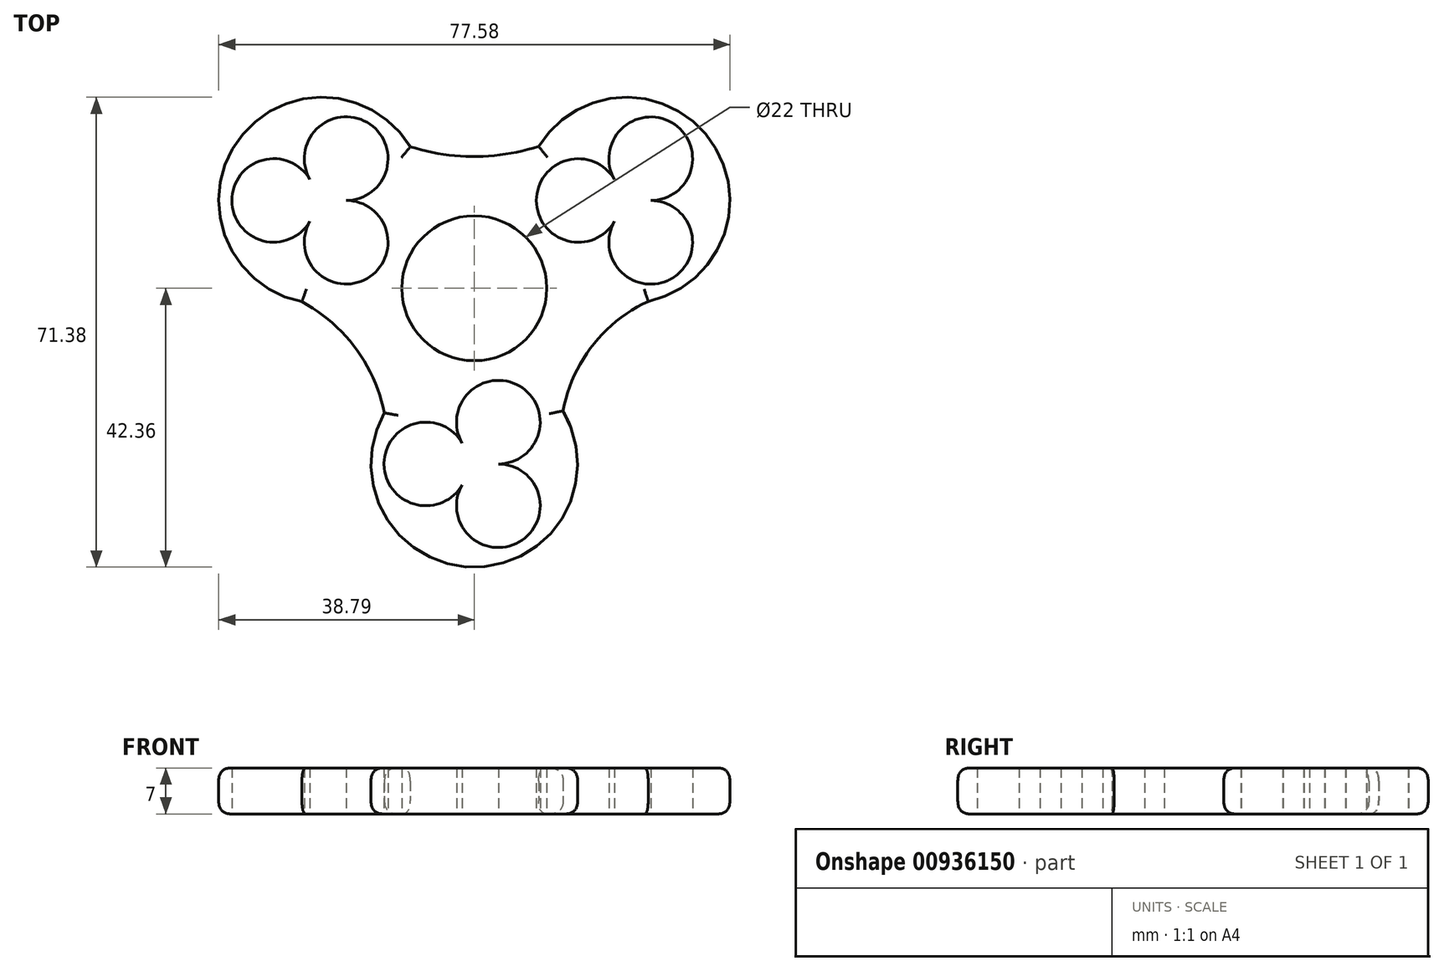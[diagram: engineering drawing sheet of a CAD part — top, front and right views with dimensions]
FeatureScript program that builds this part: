
annotation { "Feature Type Name" : "Feature", "Feature Type Description" : "" }
export const myFeature = defineFeature(function(context is Context, id is Id, definition is map)
    precondition{}
    {
        {
            var Q0;
            Q0=qCreatedBy(makeId("Top.planeOp"),FACE);
            var sketch = newSketch(context, id + "F0", { "sketchPlane" : qUnion([Q0])});
            skCircle(sketch, "E0", {"center": v(0, 0) * mm, "radius": 11 * mm});
            skPoint(sketch, "E1", {"position": v(0, -26.68) * mm});
            skCircle(sketch, "E2", {"center": v(0, -26.68) * mm, "radius": 13.68 * mm});
            skCircle(sketch, "E3.1.0", {"center": v(23.1, 13.34) * mm, "radius": 13.68 * mm});
            skCircle(sketch, "E3.2.0", {"center": v(-23.1, 13.34) * mm, "radius": 13.68 * mm});
            skCircle(sketch, "E4", {"center": v(0, -26.68) * mm, "radius": 15.68 * mm});
            skCircle(sketch, "E5.1.0", {"center": v(23.1, 13.34) * mm, "radius": 15.68 * mm});
            skCircle(sketch, "E5.2.0", {"center": v(-23.1, 13.34) * mm, "radius": 15.68 * mm});
            skPoint(sketch, "E6.endSnap0", {"position": v(0, 13.34) * mm});
            skArc(sketch, "E7", {"start": v(-9.72, 21.5) * mm, "mid": v(0.02, 20.01) * mm, "end": v(9.75, 21.56) * mm});
            skArc(sketch, "E8", {"start": v(26.39, -2) * mm, "mid": v(17.9, -8.75) * mm, "end": v(13.46, -18.64) * mm});
            skArc(sketch, "E9", {"start": v(-13.64, -18.94) * mm, "mid": v(-18.02, -9.1) * mm, "end": v(-26.15, -2.04) * mm});
            skPoint(sketch, "E10.end.orphan", {"position": v(30.3, 13.34) * mm});
            skPoint(sketch, "E6.end.orphan", {"position": v(7.43, 13.34) * mm});
            skPoint(sketch, "E11", {"position": v(6.84, -26.68) * mm});
            skPoint(sketch, "E12", {"position": v(-3.42, -32.6) * mm});
            skPoint(sketch, "E13", {"position": v(-2.54, -23.28) * mm});
            skPoint(sketch, "E14.center.orphan", {"position": v(-2.54, -26.17) * mm});
            skPoint(sketch, "E15.end.orphan", {"position": v(13.68, -26.68) * mm});
            skPoint(sketch, "E16.end.orphan", {"position": v(-6.84, -38.53) * mm});
            skLineSegment(sketch, "E17", {"start": v(-36.79, 13.34) * mm, "end": v(-23.1, 13.34) * mm});
            skPoint(sketch, "E18", {"position": v(-30.44, 13.34) * mm});
            skCircle(sketch, "E19", {"center": v(-30.44, 13.34) * mm, "radius": 6.35 * mm});
            skLineSegment(sketch, "E20", {"start": v(-23.1, 13.34) * mm, "end": v(-16.23, 25.25) * mm});
            skLineSegment(sketch, "E21", {"start": v(-23.1, 13.34) * mm, "end": v(-16.27, 1.5) * mm});
            skPoint(sketch, "E22", {"position": v(-19.44, 19.7) * mm});
            skPoint(sketch, "E23", {"position": v(-19.44, 7) * mm});
            skCircle(sketch, "E24", {"center": v(-19.44, 7) * mm, "radius": 6.35 * mm});
            skCircle(sketch, "E25", {"center": v(-19.44, 19.7) * mm, "radius": 6.35 * mm});
            skCircle(sketch, "E26.1.0", {"center": v(-7.35, -26.7) * mm, "radius": 6.35 * mm});
            skCircle(sketch, "E26.1.1", {"center": v(3.65, -33.04) * mm, "radius": 6.35 * mm});
            skCircle(sketch, "E26.1.2", {"center": v(3.65, -20.34) * mm, "radius": 6.35 * mm});
            skCircle(sketch, "E26.2.0", {"center": v(26.77, 6.97) * mm, "radius": 6.35 * mm});
            skCircle(sketch, "E26.2.1", {"center": v(26.77, 19.67) * mm, "radius": 6.35 * mm});
            skCircle(sketch, "E26.2.2", {"center": v(15.77, 13.32) * mm, "radius": 6.35 * mm});
            skSolve(sketch);
        }
        {
            var Q0;
            {var subQ4=sQuery(id+"F0.wireOp",EDGE,"E5.2.0");var subQ5=makeQuery(id+"F0.imprint","INTERSECT",VERTEX,{"derivedFrom":[subQ4,sQuery(id+"F0.wireOp",EDGE,"E9")]});Q0=makeQuery(id+"F0.imprint","IMPRINT",FACE,{"disambiguationData":[TD([[makeQuery(id+"F0.imprint","IMPRINT",EDGE,{"disambiguationData":[TD([[subQ5,-1.0]])],"derivedFrom":subQ4}),1.0]])]});}
            var Q1;
            {var subQ0=sQuery(id+"F0.wireOp",EDGE,"E19");var subQ1=sQuery(id+"F0.wireOp",EDGE,"E3.2.0");var subQ2=makeQuery(id+"F0.imprint","INTERSECT",VERTEX,{"disambiguationData":[OD(0.0)],"derivedFrom":[subQ1,subQ0]});Q1=makeQuery(id+"F0.imprint","IMPRINT",FACE,{"disambiguationData":[TD([[makeQuery(id+"F0.imprint","IMPRINT",EDGE,{"disambiguationData":[TD([[subQ2,1.0]])],"derivedFrom":subQ0}),-1.0]])]});}
            var Q2;
            {var subQ0=sQuery(id+"F0.wireOp",EDGE,"E24");var subQ3=sQuery(id+"F0.wireOp",EDGE,"E25");var subQ5=makeQuery(id+"F0.imprint","INTERSECT",VERTEX,{"derivedFrom":[subQ0,subQ3]});Q2=makeQuery(id+"F0.imprint","IMPRINT",FACE,{"disambiguationData":[TD([[makeQuery(id+"F0.imprint","IMPRINT",EDGE,{"disambiguationData":[TD([[subQ5,1.0]])],"derivedFrom":subQ0}),-1.0]])]});}
            var Q3;
            {var subQ1=sQuery(id+"F0.wireOp",EDGE,"E3.2.0");var subQ3=sQuery(id+"F0.wireOp",EDGE,"E19");var subQ4=makeQuery(id+"F0.imprint","INTERSECT",VERTEX,{"disambiguationData":[OD(1.0)],"derivedFrom":[subQ1,subQ3]});Q3=makeQuery(id+"F0.imprint","IMPRINT",FACE,{"disambiguationData":[TD([[makeQuery(id+"F0.imprint","IMPRINT",EDGE,{"disambiguationData":[TD([[subQ4,-1.0]])],"derivedFrom":subQ3}),-1.0]])]});}
            var Q4;
            {var subQ0=sQuery(id+"F0.wireOp",EDGE,"E7");Q4=makeQuery(id+"F0.imprint","IMPRINT",FACE,{"disambiguationData":[TD([[makeQuery(id+"F0.imprint","IMPRINT",EDGE,{"derivedFrom":subQ0}),-1.0]])]});}
            var Q5;
            {var subQ0=sQuery(id+"F0.wireOp",EDGE,"E8");Q5=makeQuery(id+"F0.imprint","IMPRINT",FACE,{"disambiguationData":[TD([[makeQuery(id+"F0.imprint","IMPRINT",EDGE,{"derivedFrom":subQ0}),-1.0]])]});}
            var Q6;
            {var subQ0=sQuery(id+"F0.wireOp",EDGE,"E9");Q6=makeQuery(id+"F0.imprint","IMPRINT",FACE,{"disambiguationData":[TD([[makeQuery(id+"F0.imprint","IMPRINT",EDGE,{"derivedFrom":subQ0}),-1.0]])]});}
            var Q7;
            Q7=makeQuery(id+"F0.imprint","IMPRINT",FACE,{"disambiguationData":[TD([[makeQuery(id+"F0.imprint","IMPRINT",EDGE,{"derivedFrom":sQuery(id+"F0.wireOp",EDGE,"E0")}),-1.0]])]});
            var Q8;
            {var subQ0=sQuery(id+"F0.wireOp",EDGE,"E26.2.2");var subQ1=sQuery(id+"F0.wireOp",EDGE,"E3.1.0");var subQ2=makeQuery(id+"F0.imprint","INTERSECT",VERTEX,{"disambiguationData":[OD(0.0)],"derivedFrom":[subQ1,subQ0]});Q8=makeQuery(id+"F0.imprint","IMPRINT",FACE,{"disambiguationData":[TD([[makeQuery(id+"F0.imprint","IMPRINT",EDGE,{"disambiguationData":[TD([[subQ2,-1.0]])],"derivedFrom":subQ1}),1.0]])]});}
            var Q9;
            {var subQ0=sQuery(id+"F0.wireOp",EDGE,"E26.2.2");var subQ1=sQuery(id+"F0.wireOp",EDGE,"E3.1.0");var subQ2=makeQuery(id+"F0.imprint","INTERSECT",VERTEX,{"disambiguationData":[OD(1.0)],"derivedFrom":[subQ1,subQ0]});Q9=makeQuery(id+"F0.imprint","IMPRINT",FACE,{"disambiguationData":[TD([[makeQuery(id+"F0.imprint","IMPRINT",EDGE,{"disambiguationData":[TD([[subQ2,1.0]])],"derivedFrom":subQ1}),1.0]])]});}
            var Q10;
            {var subQ3=sQuery(id+"F0.wireOp",EDGE,"E26.2.2");var subQ4=sQuery(id+"F0.wireOp",EDGE,"E3.1.0");var subQ5=makeQuery(id+"F0.imprint","INTERSECT",VERTEX,{"disambiguationData":[OD(0.0)],"derivedFrom":[subQ4,subQ3]});Q10=makeQuery(id+"F0.imprint","IMPRINT",FACE,{"disambiguationData":[TD([[makeQuery(id+"F0.imprint","IMPRINT",EDGE,{"disambiguationData":[TD([[subQ5,-1.0]])],"derivedFrom":subQ4}),-1.0]])]});}
            var Q11;
            {var subQ0=sQuery(id+"F0.wireOp",EDGE,"E26.1.0");var subQ1=sQuery(id+"F0.wireOp",EDGE,"E2");var subQ2=makeQuery(id+"F0.imprint","INTERSECT",VERTEX,{"disambiguationData":[OD(0.0)],"derivedFrom":[subQ1,subQ0]});Q11=makeQuery(id+"F0.imprint","IMPRINT",FACE,{"disambiguationData":[TD([[makeQuery(id+"F0.imprint","IMPRINT",EDGE,{"disambiguationData":[TD([[subQ2,-1.0]])],"derivedFrom":subQ1}),1.0]])]});}
            var Q12;
            {var subQ0=sQuery(id+"F0.wireOp",EDGE,"E26.1.0");var subQ1=sQuery(id+"F0.wireOp",EDGE,"E2");var subQ2=makeQuery(id+"F0.imprint","INTERSECT",VERTEX,{"disambiguationData":[OD(1.0)],"derivedFrom":[subQ1,subQ0]});Q12=makeQuery(id+"F0.imprint","IMPRINT",FACE,{"disambiguationData":[TD([[makeQuery(id+"F0.imprint","IMPRINT",EDGE,{"disambiguationData":[TD([[subQ2,1.0]])],"derivedFrom":subQ1}),1.0]])]});}
            var Q13;
            {var subQ3=sQuery(id+"F0.wireOp",EDGE,"E26.1.0");var subQ4=sQuery(id+"F0.wireOp",EDGE,"E2");var subQ5=makeQuery(id+"F0.imprint","INTERSECT",VERTEX,{"disambiguationData":[OD(0.0)],"derivedFrom":[subQ4,subQ3]});Q13=makeQuery(id+"F0.imprint","IMPRINT",FACE,{"disambiguationData":[TD([[makeQuery(id+"F0.imprint","IMPRINT",EDGE,{"disambiguationData":[TD([[subQ5,-1.0]])],"derivedFrom":subQ4}),-1.0]])]});}
            extrude(context, id + "F1", {"entities" : qUnion([Q0, Q1, Q2, Q3, Q4, Q5, Q6, Q7, Q8, Q9, Q10, Q11, Q12, Q13]), "depth" : 7 * mm, "offsetDistance" : 25 * mm});
        }
        {
            var Q0;
            Q0=makeQuery(id+"F1.opExtrude","CAP_EDGE",EDGE,{"disambiguationData":[OSD([sQuery(id+"F0.wireOp",EDGE,"E5.2.0")])],"isStart":false});
            var Q1;
            Q1=makeQuery(id+"F1.opExtrude","CAP_EDGE",EDGE,{"disambiguationData":[OSD([sQuery(id+"F0.wireOp",EDGE,"E7")])],"isStart":false});
            var Q2;
            Q2=makeQuery(id+"F1.opExtrude","CAP_EDGE",EDGE,{"disambiguationData":[OSD([sQuery(id+"F0.wireOp",EDGE,"E9")])],"isStart":false});
            var Q3;
            Q3=makeQuery(id+"F1.opExtrude","CAP_EDGE",EDGE,{"disambiguationData":[OSD([sQuery(id+"F0.wireOp",EDGE,"E5.1.0")])],"isStart":false});
            var Q4;
            Q4=makeQuery(id+"F1.opExtrude","CAP_EDGE",EDGE,{"disambiguationData":[OSD([sQuery(id+"F0.wireOp",EDGE,"E8")])],"isStart":false});
            var Q5;
            Q5=makeQuery(id+"F1.opExtrude","CAP_EDGE",EDGE,{"disambiguationData":[OSD([sQuery(id+"F0.wireOp",EDGE,"E4")])],"isStart":false});
            var Q6;
            Q6=makeQuery(id+"F1.opExtrude","CAP_EDGE",EDGE,{"disambiguationData":[OSD([sQuery(id+"F0.wireOp",EDGE,"E5.2.0")])],"isStart":true});
            var Q7;
            Q7=makeQuery(id+"F1.opExtrude","CAP_EDGE",EDGE,{"disambiguationData":[OSD([sQuery(id+"F0.wireOp",EDGE,"E9")])],"isStart":true});
            var Q8;
            Q8=makeQuery(id+"F1.opExtrude","CAP_EDGE",EDGE,{"disambiguationData":[OSD([sQuery(id+"F0.wireOp",EDGE,"E4")])],"isStart":true});
            var Q9;
            Q9=makeQuery(id+"F1.opExtrude","CAP_EDGE",EDGE,{"disambiguationData":[OSD([sQuery(id+"F0.wireOp",EDGE,"E8")])],"isStart":true});
            var Q10;
            Q10=makeQuery(id+"F1.opExtrude","CAP_EDGE",EDGE,{"disambiguationData":[OSD([sQuery(id+"F0.wireOp",EDGE,"E5.1.0")])],"isStart":true});
            var Q11;
            Q11=makeQuery(id+"F1.opExtrude","CAP_EDGE",EDGE,{"disambiguationData":[OSD([sQuery(id+"F0.wireOp",EDGE,"E7")])],"isStart":true});
            fillet(context, id + "F2", {"entities" : qUnion([Q0, Q1, Q2, Q3, Q4, Q5, Q6, Q7, Q8, Q9, Q10, Q11]), "radius" : 2 * mm, "rho" : 0.5, "crossSection" : FilletCrossSection.CONIC, "allowEdgeOverflow" : false});
        }
    });
